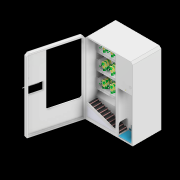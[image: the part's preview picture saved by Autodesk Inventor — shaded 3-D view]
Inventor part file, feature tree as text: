
AUTODESK INVENTOR PART (.ipt)
format: ipt  version: 2020 (Build 240168000, 168)  size: 6,999,040 bytes
history: native  units: mm
features: other x213, plane x29, helix x18, sketch x5, sweep x1, mirror x1
ambient origin geometry x8: Origin, YZ Plane, XZ Plane, XY Plane, X Axis, Y Axis, Z Axis, Center Point
bodies: Body1 (feature_tree), Body2 (feature_tree), Body3 (feature_tree), Body4 (feature_tree), Body5 (feature_tree), Body6 (feature_tree), Body7 (feature_tree), Body8 (feature_tree), Body9 (feature_tree), Body10 (feature_tree), Body11 (feature_tree), Body12 (feature_tree), Body13 (feature_tree), Body14 (feature_tree), Body15 (feature_tree), Body16 (feature_tree), Body17 (feature_tree), Body18 (feature_tree), Body19 (feature_tree), Body20 (feature_tree), Body21 (feature_tree), Body22 (feature_tree), Body23 (feature_tree), Body24 (feature_tree), Body25 (feature_tree), Body26 (feature_tree), Body27 (feature_tree), Body28 (feature_tree), Body29 (feature_tree), Body30 (feature_tree), Body31 (feature_tree), Body32 (feature_tree), Body33 (feature_tree), Body34 (feature_tree), Body35 (feature_tree), Body36 (feature_tree), Body37 (feature_tree), Body38 (feature_tree), Body39 (feature_tree), Body40 (feature_tree), Body41 (feature_tree), Body42 (feature_tree), Body43 (feature_tree), Body44 (feature_tree), Body45 (feature_tree), Body46 (feature_tree), Body47 (feature_tree), Body48 (feature_tree), Body49 (feature_tree), Body50 (feature_tree), Body51 (feature_tree), Body52 (feature_tree), Body53 (feature_tree), Body54 (feature_tree), Body55 (feature_tree), Body56 (feature_tree), Body57 (feature_tree), Body58 (feature_tree), Body59 (feature_tree), Body60 (feature_tree), Body61 (feature_tree), Body62 (feature_tree), Body63 (feature_tree), Body64 (feature_tree), Body65 (feature_tree), Body66 (feature_tree), Body67 (feature_tree), Body68 (feature_tree), Body69 (feature_tree), Body70 (feature_tree), Body71 (feature_tree), Body72 (feature_tree), Body73 (feature_tree), Body74 (feature_tree), Body75 (feature_tree), Body76 (feature_tree), Body77 (feature_tree), Body78 (feature_tree), Body79 (feature_tree), Body80 (feature_tree), Body81 (feature_tree), Body82 (feature_tree), Body83 (feature_tree), Body84 (feature_tree), Body85 (feature_tree), Body86 (feature_tree), Body87 (feature_tree), Body88 (feature_tree), Body89 (feature_tree), Body90 (feature_tree), Body91 (feature_tree), Body92 (feature_tree), Body93 (feature_tree), Body94 (feature_tree), Body95 (feature_tree), Body96 (feature_tree), Body97 (feature_tree), Body98 (feature_tree), Body99 (feature_tree), Body100 (feature_tree), Body101 (feature_tree), Body102 (feature_tree), Body103 (feature_tree), Body104 (feature_tree), Body105 (feature_tree), Body106 (feature_tree), Body107 (feature_tree)
feature tree (267):
  other  "自動販賣機2.2.iam"
  other  "上滑軌.ipt:1"
  other  "上滑軌輪.ipt:1"
  other  "下滑軌.ipt:1"
  other  "下滑軌輪.ipt:1"
  other  "本體.ipt:1"
  other  "置物架.ipt:1"
  other  "滾筒.ipt:1"
  other  "蓋.ipt:1"
  other  "鎖點支架.ipt:1"
  other  "鎖點支架.ipt:2"
  other  "鎖點支架.ipt:3"
  other  "鎖點支架.ipt:4"
  other  "鎖點支架.ipt:5"
  other  "鎖點支架.ipt:6"
  other  "下滑軌.ipt:2"
  other  "下滑軌輪.ipt:2"
  other  "下滑軌.ipt:3"
  other  "下滑軌輪.ipt:3"
  other  "下支架右.ipt:1"
  other  "下滑軌輪.ipt:4"
  other  "下支架右.ipt:2"
  other  "下滑軌輪.ipt:5"
  other  "下支架右.ipt:3"
  other  "下滑軌輪.ipt:6"
  other  "上滑軌右.ipt:1"
  other  "上滑軌輪.ipt:2"
  other  "上滑軌.ipt:2"
  other  "上滑軌輪.ipt:3"
  other  "置物架.ipt:2"
  other  "上滑軌右.ipt:2"
  other  "上滑軌輪.ipt:4"
  other  "上滑軌.ipt:3"
  other  "上滑軌輪.ipt:5"
  other  "置物架.ipt:3"
  other  "上滑軌右.ipt:3"
  other  "上滑軌輪.ipt:6"
  other  "滾筒.ipt:2"
  other  "滾筒.ipt:3"
  other  "滾筒.ipt:4"
  other  "滾筒.ipt:5"
  other  "滾筒.ipt:6"
  other  "滾筒.ipt:7"
  other  "滾筒.ipt:8"
  other  "滾筒.ipt:9"
  other  "滾筒.ipt:10"
  other  "蝸桿支架.ipt:1"
  other  "蝸桿滑塊.ipt:1"
  other  "短蝸桿.ipt:1"
  other  "長蝸桿.ipt:1"
  other  "位移平台.ipt:1"
  other  "取物窗.ipt:1"
  helix  "螺旋鉤子.ipt:1"  [1 undecoded]
  helix  "螺旋鉤子底座.ipt:1"  [1 undecoded]
  helix  "螺旋鉤子.ipt:2"  [1 undecoded]
  helix  "螺旋鉤子底座.ipt:2"  [1 undecoded]
  helix  "螺旋鉤子.ipt:3"  [1 undecoded]
  helix  "螺旋鉤子底座.ipt:3"  [1 undecoded]
  helix  "螺旋鉤子.ipt:4"  [1 undecoded]
  helix  "螺旋鉤子底座.ipt:4"  [1 undecoded]
  helix  "螺旋鉤子.ipt:5"  [1 undecoded]
  helix  "螺旋鉤子底座.ipt:5"  [1 undecoded]
  helix  "螺旋鉤子.ipt:6"  [1 undecoded]
  helix  "螺旋鉤子底座.ipt:6"  [1 undecoded]
  helix  "螺旋鉤子.ipt:7"  [1 undecoded]
  helix  "螺旋鉤子底座.ipt:7"  [1 undecoded]
  helix  "螺旋鉤子.ipt:8"  [1 undecoded]
  helix  "螺旋鉤子底座.ipt:8"  [1 undecoded]
  helix  "螺旋鉤子.ipt:9"  [1 undecoded]
  helix  "螺旋鉤子底座.ipt:9"  [1 undecoded]
  other  "名牌1.ipt:1"
  other  "名牌2.ipt:1"
  other  "名牌3.ipt:1"
  other  "名牌4.ipt:1"
  other  "名牌5.ipt:1"
  other  "名牌6.ipt:1"
  other  "名牌7.ipt:1"
  other  "名牌8.ipt:1"
  other  "名牌9.ipt:1"
  other  "模擬商品.ipt:1"
  other  "模擬錢幣.ipt:1"
  other  "模擬商品.ipt:2"
  other  "模擬商品.ipt:3"
  other  "模擬商品.ipt:4"
  other  "模擬商品.ipt:5"
  other  "模擬商品.ipt:6"
  other  "模擬商品.ipt:7"
  other  "模擬商品.ipt:8"
  other  "模擬商品.ipt:9"
  other  "模擬商品.ipt:10"
  other  "模擬商品.ipt:11"
  other  "模擬商品.ipt:12"
  other  "模擬商品.ipt:13"
  other  "模擬商品.ipt:14"
  other  "模擬商品.ipt:15"
  other  "模擬商品.ipt:16"
  other  "模擬商品.ipt:17"
  other  "模擬商品.ipt:18"
  other  "模擬商品.ipt:19"
  other  "模擬商品.ipt:20"
  other  "模擬商品.ipt:21"
  other  "模擬商品.ipt:22"
  other  "模擬商品.ipt:23"
  other  "模擬商品.ipt:24"
  other  "模擬商品.ipt:25"
  other  "模擬商品.ipt:26"
  other  "模擬商品.ipt:27"
  other  "實體1"
  sketch  "草圖21"
  plane  "工作平面28"
  sweep  "掃掠1"
  plane  "工作平面29"
  mirror  "鏡射1"
  sketch  "草圖23"
  other  "實體2"
  other  "實體3"
  other  "實體4"
  other  "實體5"
  other  "實體6"
  other  "實體7"
  other  "實體8"
  other  "實體9"
  other  "實體10"
  other  "實體11"
  other  "實體12"
  other  "實體13"
  other  "實體14"
  other  "實體15"
  other  "實體16"
  other  "實體17"
  other  "實體18"
  other  "實體19"
  other  "實體20"
  other  "實體21"
  other  "實體22"
  other  "實體23"
  other  "實體24"
  other  "實體25"
  other  "實體26"
  other  "實體27"
  other  "實體28"
  other  "實體29"
  other  "實體30"
  other  "實體31"
  other  "實體32"
  other  "實體33"
  other  "實體34"
  other  "實體35"
  other  "實體36"
  other  "實體37"
  other  "實體38"
  other  "實體39"
  other  "實體40"
  other  "實體41"
  other  "實體42"
  other  "實體43"
  other  "實體44"
  other  "實體45"
  other  "實體46"
  other  "實體47"
  other  "實體48"
  other  "實體49"
  other  "實體50"
  other  "實體51"
  other  "實體52"
  sketch  "草圖12"
  sketch  "草圖13"
  plane  "工作平面1"
  plane  "工作平面2"
  plane  "工作平面3"
  other  "實體53"
  other  "實體54"
  other  "草圖12_1"
  other  "草圖13_1"
  plane  "工作平面1_1"
  plane  "工作平面2_1"
  plane  "工作平面3_1"
  other  "實體55"
  other  "實體56"
  other  "草圖12_2"
  other  "草圖13_2"
  plane  "工作平面1_2"
  plane  "工作平面2_2"
  plane  "工作平面3_2"
  other  "實體57"
  other  "實體58"
  other  "草圖12_3"
  other  "草圖13_3"
  plane  "工作平面1_3"
  plane  "工作平面2_3"
  plane  "工作平面3_3"
  other  "實體59"
  other  "實體60"
  other  "草圖12_4"
  other  "草圖13_4"
  plane  "工作平面1_4"
  plane  "工作平面2_4"
  plane  "工作平面3_4"
  other  "實體61"
  other  "實體62"
  other  "草圖12_5"
  other  "草圖13_5"
  plane  "工作平面1_5"
  plane  "工作平面2_5"
  plane  "工作平面3_5"
  other  "實體63"
  other  "實體64"
  other  "草圖12_6"
  other  "草圖13_6"
  plane  "工作平面1_6"
  plane  "工作平面2_6"
  plane  "工作平面3_6"
  other  "實體65"
  other  "實體66"
  other  "草圖12_7"
  other  "草圖13_7"
  plane  "工作平面1_7"
  plane  "工作平面2_7"
  plane  "工作平面3_7"
  other  "實體67"
  other  "實體68"
  other  "草圖12_8"
  other  "草圖13_8"
  plane  "工作平面1_8"
  plane  "工作平面2_8"
  plane  "工作平面3_8"
  other  "實體69"
  other  "實體70"
  other  "實體71"
  other  "實體72"
  other  "實體73"
  other  "實體74"
  other  "實體75"
  other  "實體76"
  other  "實體77"
  other  "實體78"
  other  "實體79"
  other  "實體80"
  other  "實體81"
  other  "實體82"
  other  "實體83"
  other  "實體84"
  other  "實體85"
  other  "實體86"
  other  "實體87"
  other  "實體88"
  other  "實體89"
  other  "實體90"
  other  "實體91"
  other  "實體92"
  other  "實體93"
  other  "實體94"
  other  "實體95"
  other  "實體96"
  other  "實體97"
  other  "實體98"
  other  "實體99"
  other  "實體100"
  other  "實體101"
  other  "實體102"
  other  "實體103"
  other  "實體104"
  other  "實體105"
  other  "實體106"
  sketch  "草圖22"
  other  "實體107"
  other  "投影切割邊1"
note: 18 required parameter values undecoded (feature->parameter linkage not recoverable at this tier; creation-order binding heuristic only, values carry confidence <= 0.55)
